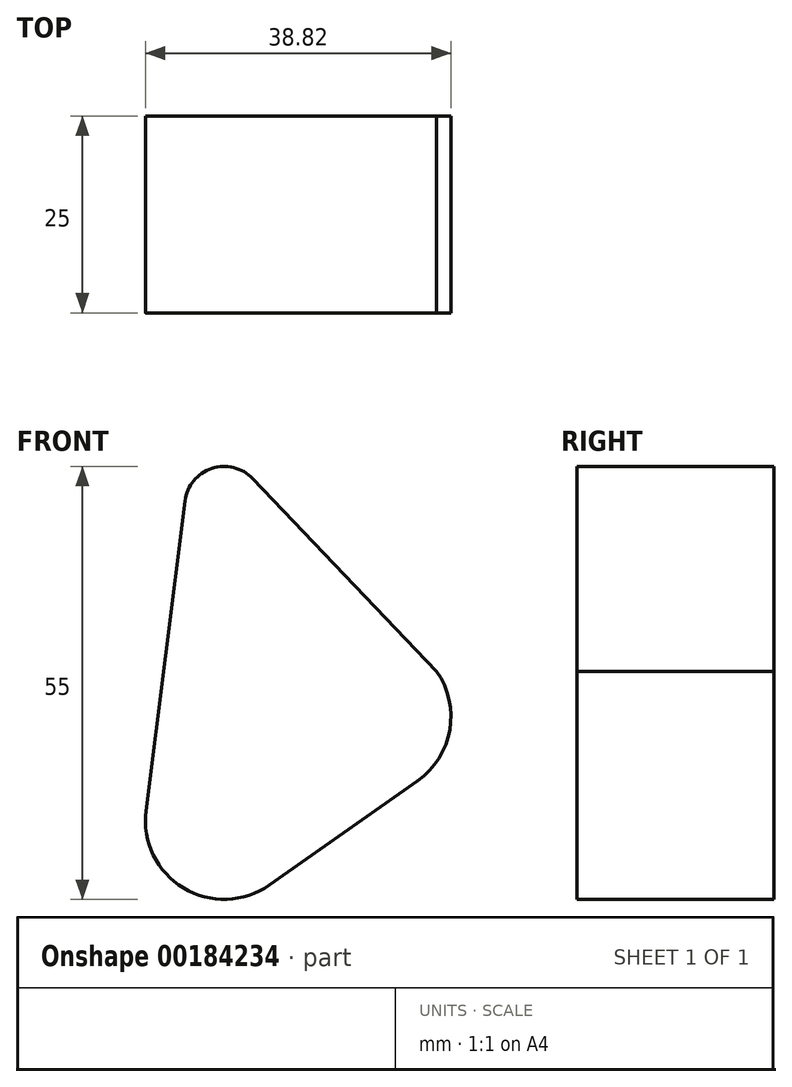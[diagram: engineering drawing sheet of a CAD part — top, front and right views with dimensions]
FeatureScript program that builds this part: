
annotation { "Feature Type Name" : "Feature", "Feature Type Description" : "" }
export const myFeature = defineFeature(function(context is Context, id is Id, definition is map)
    precondition{}
    {
        {
            var Q0;
            Q0=qCreatedBy(makeId("Front.planeOp"),FACE);
            var sketch = newSketch(context, id + "F0", { "sketchPlane" : qUnion([Q0])});
            skLineSegment(sketch, "E0", {"start": v(0, 0) * mm, "end": v(0, 40) * mm});
            skLineSegment(sketch, "E1", {"start": v(0, 0) * mm, "end": v(18.82, 13.23) * mm});
            skLineSegment(sketch, "E2", {"start": v(0, 40) * mm, "end": v(18.82, 13.22) * mm});
            skCircle(sketch, "E3", {"center": v(0, 40) * mm, "radius": 5 * mm});
            skCircle(sketch, "E4", {"center": v(0, 0) * mm, "radius": 10 * mm});
            skCircle(sketch, "E5", {"center": v(18.82, 13.23) * mm, "radius": 10 * mm});
            skLineSegment(sketch, "E6", {"start": v(-4.96, 40.62) * mm, "end": v(-9.92, 1.25) * mm});
            skLineSegment(sketch, "E7", {"start": v(18.82, 13.23) * mm, "end": v(27, 18.98) * mm});
            skLineSegment(sketch, "E8", {"start": v(27, 18.97) * mm, "end": v(3.62, 43.45) * mm});
            skLineSegment(sketch, "E9", {"start": v(0, 0) * mm, "end": v(5.75, -8.18) * mm});
            skLineSegment(sketch, "E10", {"start": v(18.82, 13.23) * mm, "end": v(24.57, 5.04) * mm});
            skLineSegment(sketch, "E11", {"start": v(24.57, 5.04) * mm, "end": v(5.75, -8.18) * mm});
            skPoint(sketch, "E12", {"position": v(0, 20) * mm});
            skSolve(sketch);
        }
        {
            var Q0;
            {var subQ0=sQuery(id+"F0.wireOp",EDGE,"0x1H2vVZ-09zE-qG4Q-aBR2-LtjDIM7oajvk");Q0=makeQuery(id+"F0.imprint","IMPRINT",FACE,{"disambiguationData":[TD([[makeQuery(id+"F0.imprint","IMPRINT",EDGE,{"derivedFrom":subQ0}),1.0]])]});}
            var Q1;
            {var subQ0=sQuery(id+"F0.wireOp",EDGE,"E3");var subQ1=sQuery(id+"F0.wireOp",EDGE,"E2");var subQ2=makeQuery(id+"F0.imprint","INTERSECT",VERTEX,{"derivedFrom":[subQ1,subQ0]});Q1=makeQuery(id+"F0.imprint","IMPRINT",FACE,{"disambiguationData":[TD([[makeQuery(id+"F0.imprint","IMPRINT",EDGE,{"disambiguationData":[TD([[subQ2,-1.0]])],"derivedFrom":subQ1}),1.0]])]});}
            var Q2;
            {var subQ0=sQuery(id+"F0.wireOp",EDGE,"0x1H2vVZ-09zE-qG4Q-aBR2-LtjDIM7oajvk");Q2=makeQuery(id+"F0.imprint","IMPRINT",FACE,{"disambiguationData":[TD([[makeQuery(id+"F0.imprint","IMPRINT",EDGE,{"derivedFrom":subQ0}),-1.0]])]});}
            var Q3;
            {var subQ0=sQuery(id+"F0.wireOp",EDGE,"E4");var subQ1=sQuery(id+"F0.wireOp",EDGE,"E0");var subQ2=makeQuery(id+"F0.imprint","INTERSECT",VERTEX,{"derivedFrom":[subQ1,subQ0]});Q3=makeQuery(id+"F0.imprint","IMPRINT",FACE,{"disambiguationData":[TD([[makeQuery(id+"F0.imprint","IMPRINT",EDGE,{"disambiguationData":[TD([[subQ2,-1.0]])],"derivedFrom":subQ1}),1.0]])]});}
            var Q4;
            {var subQ1=sQuery(id+"F0.wireOp",EDGE,"E0");var subQ7=sQuery(id+"F0.wireOp",EDGE,"E4");var subQ11=makeQuery(id+"F0.imprint","INTERSECT",VERTEX,{"derivedFrom":[subQ1,subQ7]});Q4=makeQuery(id+"F0.imprint","IMPRINT",FACE,{"disambiguationData":[TD([[makeQuery(id+"F0.imprint","IMPRINT",EDGE,{"disambiguationData":[TD([[subQ11,-1.0]])],"derivedFrom":subQ1}),-1.0]])]});}
            var Q5;
            {var subQ1=sQuery(id+"F0.wireOp",EDGE,"E0");var subQ3=sQuery(id+"F0.wireOp",EDGE,"E3");var subQ4=makeQuery(id+"F0.imprint","INTERSECT",VERTEX,{"derivedFrom":[subQ1,subQ3]});Q5=makeQuery(id+"F0.imprint","IMPRINT",FACE,{"disambiguationData":[TD([[makeQuery(id+"F0.imprint","IMPRINT",EDGE,{"disambiguationData":[TD([[subQ4,-1.0]])],"derivedFrom":subQ3}),1.0]])]});}
            var Q6;
            {var subQ3=sQuery(id+"F0.wireOp",EDGE,"E0");var subQ7=sQuery(id+"F0.wireOp",EDGE,"E1");var subQ8=makeQuery(id+"F0.imprint","INTERSECT",VERTEX,{"derivedFrom":[subQ3,subQ7]});Q6=makeQuery(id+"F0.imprint","IMPRINT",FACE,{"disambiguationData":[TD([[makeQuery(id+"F0.imprint","IMPRINT",EDGE,{"disambiguationData":[TD([[subQ8,-1.0]])],"derivedFrom":subQ3}),1.0]])]});}
            var Q7;
            {var subQ0=sQuery(id+"F0.wireOp",EDGE,"E1");var subQ1=sQuery(id+"F0.wireOp",EDGE,"E0");var subQ2=makeQuery(id+"F0.imprint","INTERSECT",VERTEX,{"derivedFrom":[subQ1,subQ0]});Q7=makeQuery(id+"F0.imprint","IMPRINT",FACE,{"disambiguationData":[TD([[makeQuery(id+"F0.imprint","IMPRINT",EDGE,{"disambiguationData":[TD([[subQ2,-1.0]])],"derivedFrom":subQ1}),-1.0]])]});}
            var Q8;
            {var subQ5=sQuery(id+"F0.wireOp",EDGE,"VQ8rFFLu-R7WQ-lXkn-5q1E-jqRUfciuClUJ");Q8=makeQuery(id+"F0.imprint","IMPRINT",FACE,{"disambiguationData":[TD([[makeQuery(id+"F0.imprint","IMPRINT",EDGE,{"derivedFrom":subQ5}),1.0]])]});}
            var Q9;
            {var subQ0=sQuery(id+"F0.wireOp",EDGE,"E7");Q9=makeQuery(id+"F0.imprint","IMPRINT",FACE,{"disambiguationData":[TD([[makeQuery(id+"F0.imprint","IMPRINT",EDGE,{"derivedFrom":subQ0}),-1.0]])]});}
            var Q10;
            {var subQ1=sQuery(id+"F0.wireOp",EDGE,"E1");var subQ3=sQuery(id+"F0.wireOp",EDGE,"E5");var subQ4=makeQuery(id+"F0.imprint","INTERSECT",VERTEX,{"derivedFrom":[subQ1,subQ3]});Q10=makeQuery(id+"F0.imprint","IMPRINT",FACE,{"disambiguationData":[TD([[makeQuery(id+"F0.imprint","IMPRINT",EDGE,{"disambiguationData":[TD([[subQ4,1.0]])],"derivedFrom":subQ3}),1.0]])]});}
            var Q11;
            {var subQ0=sQuery(id+"F0.wireOp",EDGE,"E7");Q11=makeQuery(id+"F0.imprint","IMPRINT",FACE,{"disambiguationData":[TD([[makeQuery(id+"F0.imprint","IMPRINT",EDGE,{"derivedFrom":subQ0}),1.0]])]});}
            var Q12;
            {var subQ5=sQuery(id+"F0.wireOp",EDGE,"E11");Q12=makeQuery(id+"F0.imprint","IMPRINT",FACE,{"disambiguationData":[TD([[makeQuery(id+"F0.imprint","IMPRINT",EDGE,{"derivedFrom":subQ5}),-1.0]])]});}
            var Q13;
            {var subQ0=sQuery(id+"F0.wireOp",EDGE,"E9");Q13=makeQuery(id+"F0.imprint","IMPRINT",FACE,{"disambiguationData":[TD([[makeQuery(id+"F0.imprint","IMPRINT",EDGE,{"derivedFrom":subQ0}),1.0]])]});}
            var Q14;
            {var subQ0=sQuery(id+"F0.wireOp",EDGE,"E10");Q14=makeQuery(id+"F0.imprint","IMPRINT",FACE,{"disambiguationData":[TD([[makeQuery(id+"F0.imprint","IMPRINT",EDGE,{"derivedFrom":subQ0}),-1.0]])]});}
            var Q15;
            {var subQ2=sQuery(id+"F0.wireOp",EDGE,"E0");var subQ5=sQuery(id+"F0.wireOp",EDGE,"E2");var subQ6=makeQuery(id+"F0.imprint","INTERSECT",VERTEX,{"derivedFrom":[subQ2,subQ5]});Q15=makeQuery(id+"F0.imprint","IMPRINT",FACE,{"disambiguationData":[TD([[makeQuery(id+"F0.imprint","IMPRINT",EDGE,{"disambiguationData":[TD([[subQ6,1.0]])],"derivedFrom":subQ2}),1.0]])]});}
            extrude(context, id + "F1", {"entities" : qUnion([Q0, Q1, Q2, Q3, Q4, Q5, Q6, Q7, Q8, Q9, Q10, Q11, Q12, Q13, Q14, Q15]), "depth" : 25 * mm});
        }
    });
